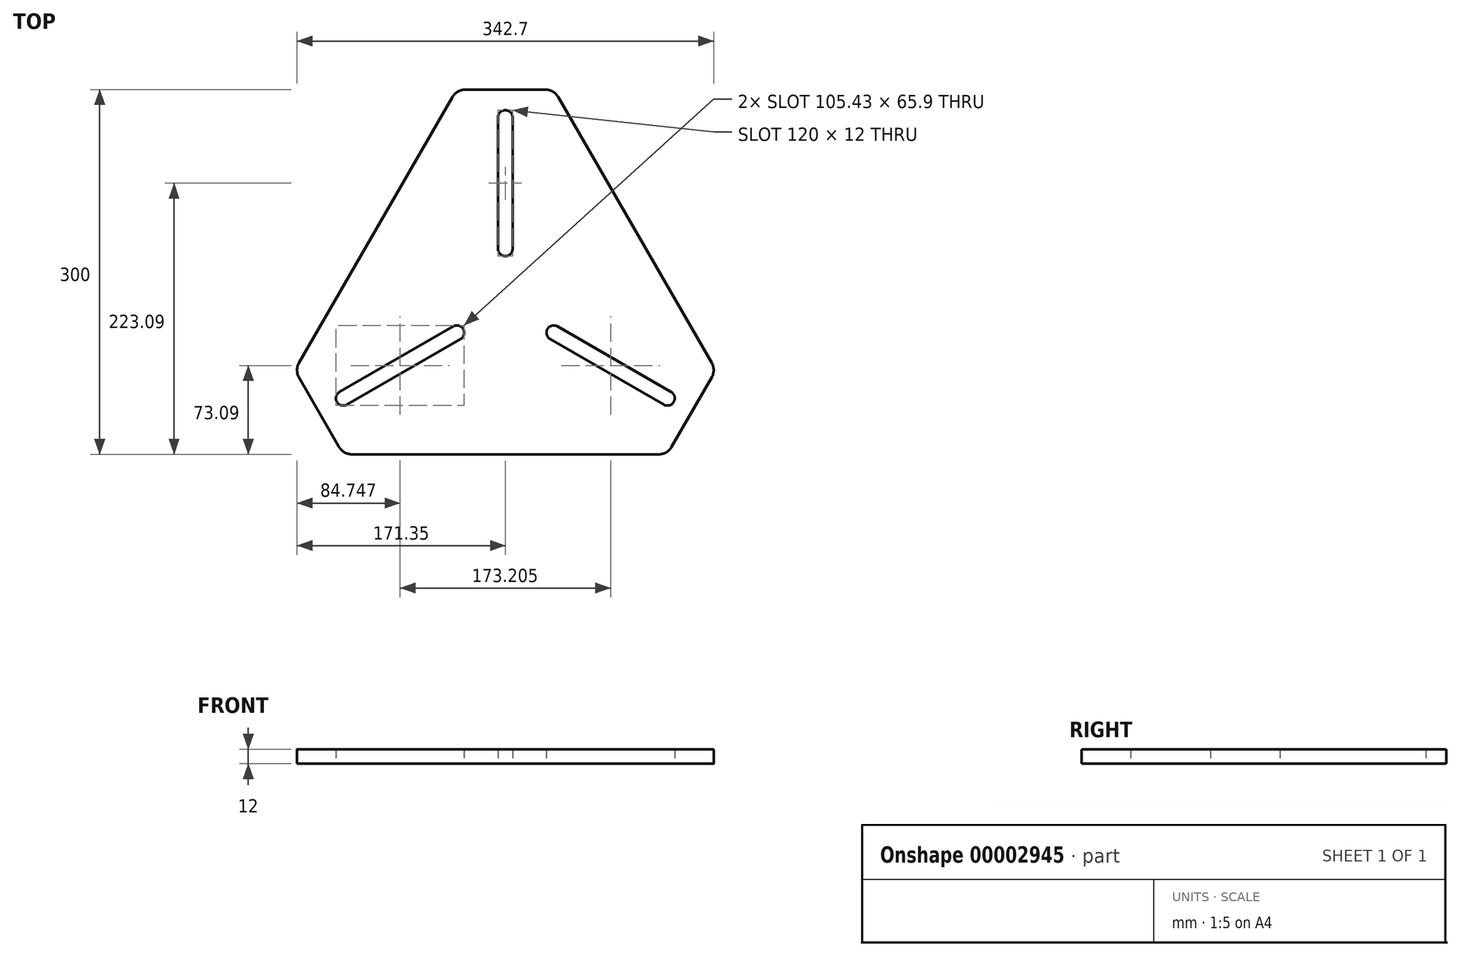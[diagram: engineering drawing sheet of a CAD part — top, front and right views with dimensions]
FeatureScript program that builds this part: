
annotation { "Feature Type Name" : "Feature", "Feature Type Description" : "" }
export const myFeature = defineFeature(function(context is Context, id is Id, definition is map)
    precondition{}
    {
        {
            var Q0;
            Q0=qCreatedBy(makeId("Top.planeOp"),FACE);
            var sketch = newSketch(context, id + "F0", { "sketchPlane" : qUnion([Q0])});
            skLineSegment(sketch, "E0", {"start": v(-12.11, 223.1) * mm, "end": v(-12.11, 239.6) * mm, "construction": true});
            skLineSegment(sketch, "E1", {"start": v(-12.11, 239.6) * mm, "end": v(-11.22, 239.6) * mm, "construction": true});
            skLineSegment(sketch, "E2", {"start": v(-11.22, 239.6) * mm, "end": v(-11.22, 260.23) * mm, "construction": true});
            skLineSegment(sketch, "E3", {"start": v(-11.22, 260.23) * mm, "end": v(12.3, 260.23) * mm, "construction": true});
            skLineSegment(sketch, "E4", {"start": v(12.3, 260.23) * mm, "end": v(12.3, 239.6) * mm, "construction": true});
            skLineSegment(sketch, "E5", {"start": v(12.3, 239.6) * mm, "end": v(13.2, 239.6) * mm, "construction": true});
            skLineSegment(sketch, "E6", {"start": v(13.2, 239.6) * mm, "end": v(13.2, 223.1) * mm, "construction": true});
            skLineSegment(sketch, "E7", {"start": v(13.2, 223.1) * mm, "end": v(4.67, 223.1) * mm, "construction": true});
            skLineSegment(sketch, "E8", {"start": v(-3.58, 223.1) * mm, "end": v(-12.11, 223.1) * mm, "construction": true});
            skLineSegment(sketch, "E9", {"start": v(-3.58, 223.1) * mm, "end": v(-3.58, 218.62) * mm, "construction": true});
            skLineSegment(sketch, "E10", {"start": v(-3.58, 218.62) * mm, "end": v(-1.52, 218.62) * mm, "construction": true});
            skLineSegment(sketch, "E11", {"start": v(4.67, 218.62) * mm, "end": v(4.67, 223.1) * mm, "construction": true});
            skLineSegment(sketch, "E12", {"start": v(-1.52, 218.62) * mm, "end": v(-1.52, 207.96) * mm, "construction": true});
            skLineSegment(sketch, "E13", {"start": v(2.6, 207.96) * mm, "end": v(2.6, 218.62) * mm, "construction": true});
            skLineSegment(sketch, "E14.trimOffspring", {"start": v(2.6, 218.62) * mm, "end": v(4.67, 218.62) * mm, "construction": true});
            skLineSegment(sketch, "E15", {"start": v(-1.52, 207.96) * mm, "end": v(2.6, 207.96) * mm, "construction": true});
            skCircle(sketch, "E16", {"center": v(0, 0) * mm, "radius": 181.37 * mm, "construction": true});
            skLineSegment(sketch, "E17", {"start": v(-40, 176.9) * mm, "end": v(40, 176.9) * mm});
            skLineSegment(sketch, "E18", {"start": v(0, 176.9) * mm, "end": v(0, 0) * mm, "construction": true});
            skLineSegment(sketch, "E19", {"start": v(40, 176.9) * mm, "end": v(173.2, -53.81) * mm});
            skLineSegment(sketch, "E20", {"start": v(173.2, -53.81) * mm, "end": v(133.2, -123.1) * mm});
            skLineSegment(sketch, "E21", {"start": v(133.2, -123.1) * mm, "end": v(-133.2, -123.1) * mm});
            skLineSegment(sketch, "E22", {"start": v(-133.2, -123.1) * mm, "end": v(-173.2, -53.81) * mm});
            skLineSegment(sketch, "E23", {"start": v(-173.2, -53.81) * mm, "end": v(-40, 176.9) * mm});
            skLineSegment(sketch, "E24.rect.bottom", {"start": v(0, 40) * mm, "end": v(0, 40) * mm});
            skLineSegment(sketch, "E24.rect.top", {"start": v(0, 160) * mm, "end": v(0, 160) * mm});
            skLineSegment(sketch, "E24.rect.left", {"start": v(6, 46) * mm, "end": v(6, 154) * mm});
            skLineSegment(sketch, "E24.rect.right", {"start": v(-6, 46) * mm, "end": v(-6, 154) * mm});
            skPoint(sketch, "E24.rect.middle", {"position": v(0, 100) * mm});
            skPoint(sketch, "E25.visualSharp", {"position": v(-6, 160) * mm});
            skArc(sketch, "E25.filletArc", {"start": v(0, 160) * mm, "mid": v(-4.24, 158.24) * mm, "end": v(-6, 154) * mm});
            skPoint(sketch, "E26.visualSharp", {"position": v(6, 160) * mm});
            skArc(sketch, "E26.filletArc", {"start": v(6, 154) * mm, "mid": v(4.24, 158.24) * mm, "end": v(0, 160) * mm});
            skPoint(sketch, "E27.visualSharp", {"position": v(6, 40) * mm});
            skArc(sketch, "E27.filletArc", {"start": v(0, 40) * mm, "mid": v(4.24, 41.76) * mm, "end": v(6, 46) * mm});
            skPoint(sketch, "E28.visualSharp", {"position": v(-6, 40) * mm});
            skArc(sketch, "E28.filletArc", {"start": v(-6, 46) * mm, "mid": v(-4.24, 41.76) * mm, "end": v(0, 40) * mm});
            skPoint(sketch, "E29.1.0", {"position": v(86.6, -50) * mm});
            skLineSegment(sketch, "E29.1.1", {"start": v(42.84, -17.8) * mm, "end": v(136.37, -71.8) * mm});
            skLineSegment(sketch, "E29.1.2", {"start": v(36.84, -28.2) * mm, "end": v(130.37, -82.2) * mm});
            skArc(sketch, "E29.1.3", {"start": v(34.64, -20) * mm, "mid": v(34.04, -24.55) * mm, "end": v(36.84, -28.2) * mm});
            skArc(sketch, "E29.1.4", {"start": v(42.84, -17.8) * mm, "mid": v(38.28, -17.2) * mm, "end": v(34.64, -20) * mm});
            skArc(sketch, "E29.1.5", {"start": v(138.56, -80) * mm, "mid": v(139.16, -75.45) * mm, "end": v(136.37, -71.8) * mm});
            skArc(sketch, "E29.1.6", {"start": v(130.37, -82.2) * mm, "mid": v(134.92, -82.8) * mm, "end": v(138.56, -80) * mm});
            skPoint(sketch, "E29.2.0", {"position": v(-86.6, -50) * mm});
            skLineSegment(sketch, "E29.2.1", {"start": v(-36.84, -28.2) * mm, "end": v(-130.37, -82.2) * mm});
            skLineSegment(sketch, "E29.2.2", {"start": v(-42.84, -17.8) * mm, "end": v(-136.37, -71.8) * mm});
            skArc(sketch, "E29.2.3", {"start": v(-34.64, -20) * mm, "mid": v(-38.28, -17.2) * mm, "end": v(-42.84, -17.8) * mm});
            skArc(sketch, "E29.2.4", {"start": v(-36.84, -28.2) * mm, "mid": v(-34.04, -24.55) * mm, "end": v(-34.64, -20) * mm});
            skArc(sketch, "E29.2.5", {"start": v(-138.56, -80) * mm, "mid": v(-134.92, -82.8) * mm, "end": v(-130.37, -82.2) * mm});
            skArc(sketch, "E29.2.6", {"start": v(-136.37, -71.8) * mm, "mid": v(-139.16, -75.45) * mm, "end": v(-138.56, -80) * mm});
            skLineSegment(sketch, "E29.anchor1", {"start": v(0, 0) * mm, "end": v(0, 100) * mm, "construction": true});
            skLineSegment(sketch, "E29.anchor2", {"start": v(0, 0) * mm, "end": v(-86.6, -50) * mm, "construction": true});
            skSolve(sketch);
        }
        {
            var Q0;
            Q0=makeQuery(id+"F0.imprint","IMPRINT",FACE,{"disambiguationData":[TD([[makeQuery(id+"F0.imprint","IMPRINT",EDGE,{"derivedFrom":sQuery(id+"F0.wireOp",EDGE,"E17")}),-1.0]])]});
            extrude(context, id + "F1", {"entities" : qUnion([Q0]), "depth" : 12 * mm});
        }
        {
            var Q0;
            Q0=makeQuery(id+"F1.opExtrude","SWEPT_EDGE",EDGE,{"disambiguationData":[OSD([sQuery(id+"F0.wireOp",EDGE,"E21"),sQuery(id+"F0.wireOp",EDGE,"E22")])]});
            var Q1;
            Q1=makeQuery(id+"F1.opExtrude","SWEPT_EDGE",EDGE,{"disambiguationData":[OSD([sQuery(id+"F0.wireOp",EDGE,"E20"),sQuery(id+"F0.wireOp",EDGE,"E21")])]});
            var Q2;
            Q2=makeQuery(id+"F1.opExtrude","SWEPT_EDGE",EDGE,{"disambiguationData":[OSD([sQuery(id+"F0.wireOp",EDGE,"E19"),sQuery(id+"F0.wireOp",EDGE,"E20")])]});
            var Q3;
            Q3=makeQuery(id+"F1.opExtrude","SWEPT_EDGE",EDGE,{"disambiguationData":[OSD([sQuery(id+"F0.wireOp",EDGE,"E17"),sQuery(id+"F0.wireOp",EDGE,"E19")])]});
            var Q4;
            Q4=makeQuery(id+"F1.opExtrude","SWEPT_EDGE",EDGE,{"disambiguationData":[OSD([sQuery(id+"F0.wireOp",EDGE,"E17"),sQuery(id+"F0.wireOp",EDGE,"E23")])]});
            var Q5;
            Q5=makeQuery(id+"F1.opExtrude","SWEPT_EDGE",EDGE,{"disambiguationData":[OSD([sQuery(id+"F0.wireOp",EDGE,"E22"),sQuery(id+"F0.wireOp",EDGE,"E23")])]});
            fillet(context, id + "F2", {"entities" : qUnion([Q0, Q1, Q2, Q3, Q4, Q5]), "radius" : 12 * mm, "tangentPropagation" : true, "allowEdgeOverflow" : false});
        }
    });
